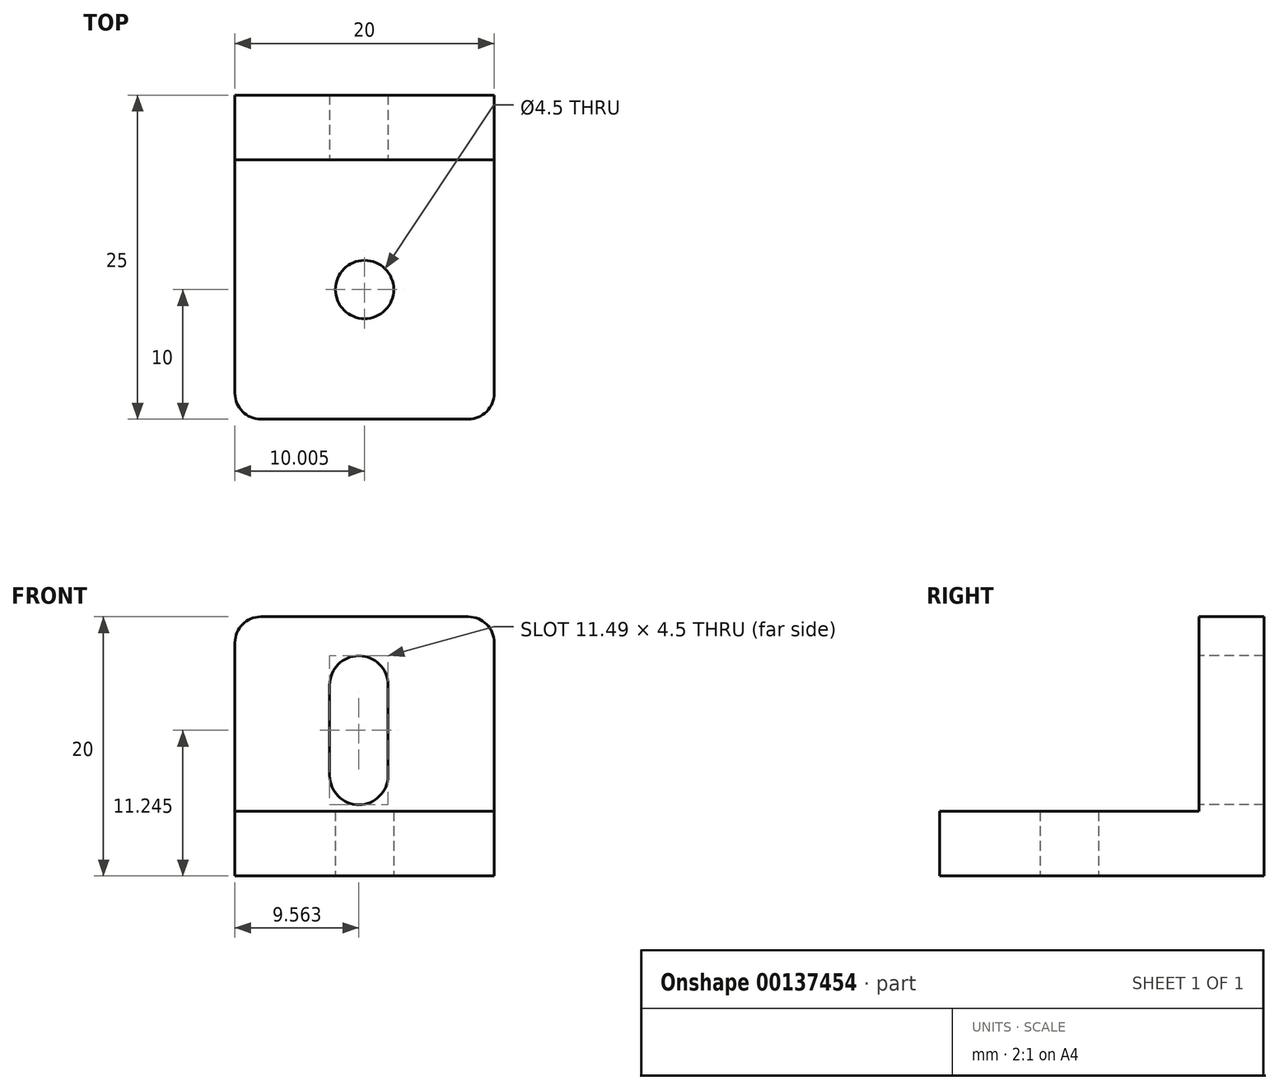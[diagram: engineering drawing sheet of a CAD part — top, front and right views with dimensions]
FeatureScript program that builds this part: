
annotation { "Feature Type Name" : "Feature", "Feature Type Description" : "" }
export const myFeature = defineFeature(function(context is Context, id is Id, definition is map)
    precondition{}
    {
        {
            var Q0;
            Q0=qCreatedBy(makeId("Top.planeOp"),FACE);
            var sketch = newSketch(context, id + "F0", { "sketchPlane" : qUnion([Q0])});
            skLineSegment(sketch, "E0.bottom", {"start": v(-9.66, 0) * mm, "end": v(10.34, 0) * mm});
            skLineSegment(sketch, "E0.top", {"start": v(-9.66, 25) * mm, "end": v(10.34, 25) * mm});
            skLineSegment(sketch, "E0.left", {"start": v(-9.66, 0) * mm, "end": v(-9.66, 25) * mm});
            skLineSegment(sketch, "E0.right", {"start": v(10.34, 0) * mm, "end": v(10.34, 25) * mm});
            skCircle(sketch, "E1", {"center": v(0.34, 10) * mm, "radius": 2.25 * mm});
            skPoint(sketch, "E2", {"position": v(0.34, 25) * mm});
            skPoint(sketch, "E3", {"position": v(-9.66, 10) * mm});
            skLineSegment(sketch, "E4", {"start": v(-9.66, 20) * mm, "end": v(10.34, 20) * mm});
            skSolve(sketch);
        }
        {
            var Q0;
            {var subQ1=sQuery(id+"F0.wireOp",EDGE,"E0.bottom");Q0=makeQuery(id+"F0.imprint","IMPRINT",FACE,{"disambiguationData":[TD([[makeQuery(id+"F0.imprint","IMPRINT",EDGE,{"derivedFrom":subQ1}),1.0]])]});}
            extrude(context, id + "F1", {"entities" : qUnion([Q0]), "depth" : 5 * mm});
        }
        {
            var Q0;
            {var subQ0=sQuery(id+"F0.wireOp",EDGE,"E0.top");Q0=makeQuery(id+"F0.imprint","IMPRINT",FACE,{"disambiguationData":[TD([[makeQuery(id+"F0.imprint","IMPRINT",EDGE,{"derivedFrom":subQ0}),-1.0]])]});}
            extrude(context, id + "F2", {"entities" : qUnion([Q0]), "operationType" : NewBodyOperationType.ADD, "depth" : 20 * mm});
        }
        {
            var Q0;
            Q0=makeQuery(id+"F2.opExtrude","SWEPT_FACE",FACE,{"disambiguationData":[OSD([sQuery(id+"F0.wireOp",EDGE,"E4")])]});
            var sketch = newSketch(context, id + "F3", { "sketchPlane" : qUnion([Q0])});
            skPoint(sketch, "E5", {"position": v(0.34, 20) * mm});
            skPoint(sketch, "E6", {"position": v(-9.66, 12.5) * mm});
            skArc(sketch, "E7", {"start": v(2.15, 14.74) * mm, "mid": v(-0.1, 17) * mm, "end": v(-2.35, 14.74) * mm});
            skArc(sketch, "E8", {"start": v(-2.35, 7.75) * mm, "mid": v(-0.1, 5.5) * mm, "end": v(2.15, 7.75) * mm});
            skLineSegment(sketch, "E9", {"start": v(2.15, 7.75) * mm, "end": v(2.15, 14.74) * mm});
            skLineSegment(sketch, "E10", {"start": v(-2.35, 7.75) * mm, "end": v(-2.35, 14.74) * mm});
            skSolve(sketch);
        }
        {
            var Q0;
            Q0=qSketchRegion(id+"F3",true);
            extrude(context, id + "F4", {"entities" : qUnion([Q0]), "operationType" : NewBodyOperationType.REMOVE, "oppositeDirection" : true, "depth" : 25 * mm});
        }
        {
            var Q0;
            Q0=makeQuery(id+"F2.opExtrude","CAP_EDGE",EDGE,{"disambiguationData":[OSD([sQuery(id+"F0.wireOp",EDGE,"E0.left")])],"isStart":false});
            var Q1;
            Q1=makeQuery(id+"F2.opExtrude","CAP_EDGE",EDGE,{"disambiguationData":[OSD([sQuery(id+"F0.wireOp",EDGE,"E0.right")])],"isStart":false});
            var Q2;
            Q2=makeQuery(id+"F1.opExtrude","SWEPT_EDGE",EDGE,{"disambiguationData":[OSD([sQuery(id+"F0.wireOp",EDGE,"E0.bottom"),sQuery(id+"F0.wireOp",EDGE,"E0.left")])]});
            var Q3;
            Q3=makeQuery(id+"F1.opExtrude","SWEPT_EDGE",EDGE,{"disambiguationData":[OSD([sQuery(id+"F0.wireOp",EDGE,"E0.bottom"),sQuery(id+"F0.wireOp",EDGE,"E0.right")])]});
            var Q4;
            Q4=makeQuery(id+"F1.opExtrude","CAP_EDGE",EDGE,{"disambiguationData":[OSD([sQuery(id+"F0.wireOp",EDGE,"E4")])],"isStart":false});
            fillet(context, id + "F5", {"entities" : qUnion([Q0, Q1, Q2, Q3, Q4]), "radius" : 2 * mm, "tangentPropagation" : true, "allowEdgeOverflow" : false});
        }
    });
